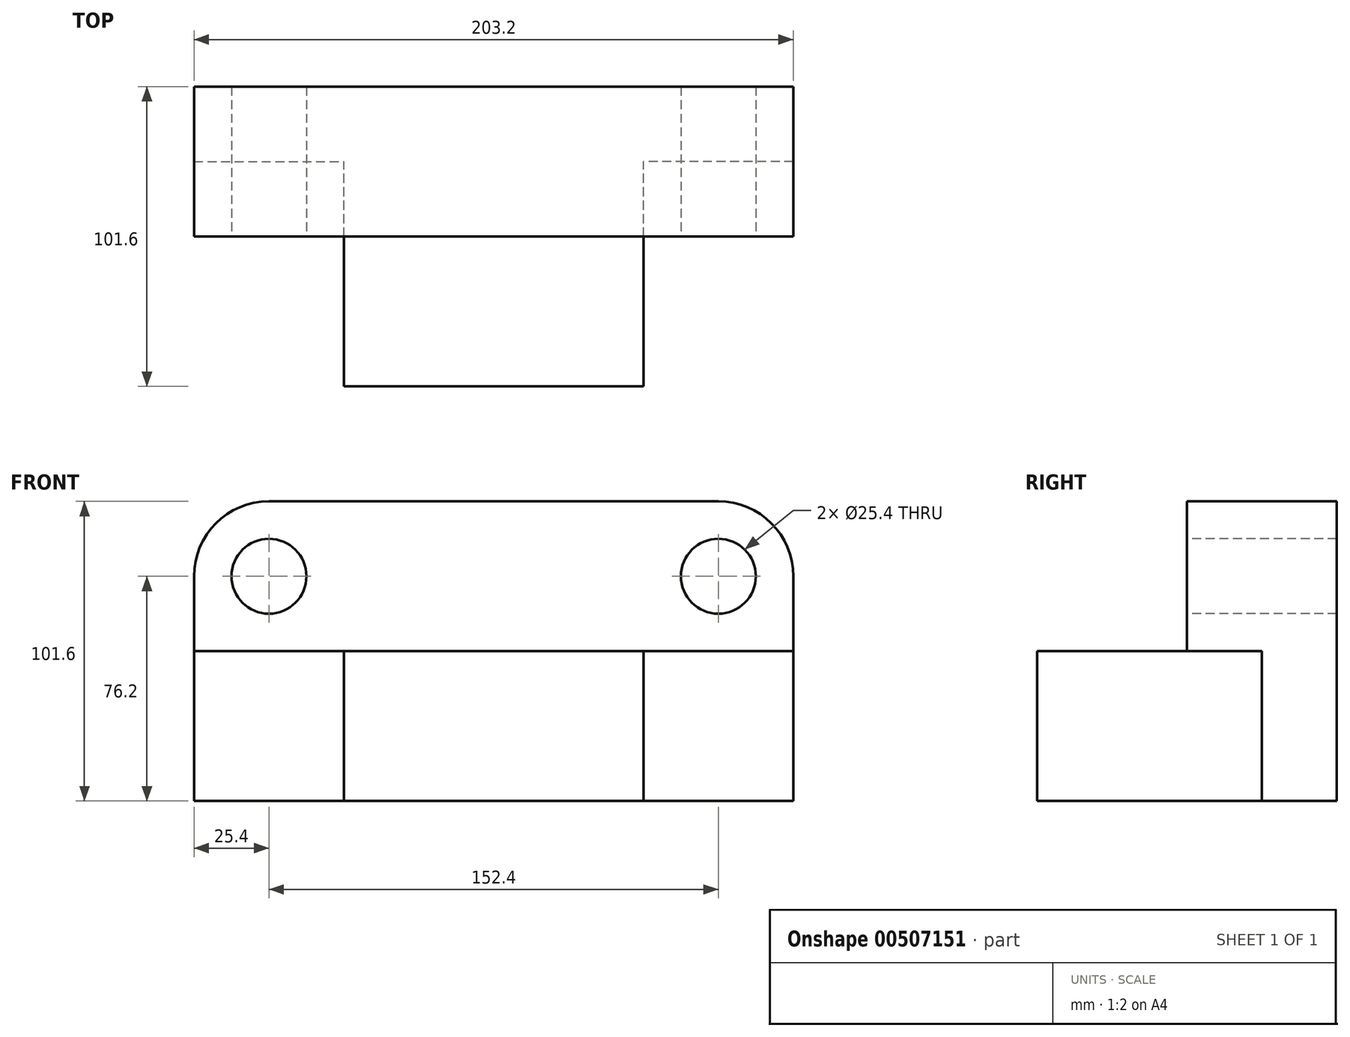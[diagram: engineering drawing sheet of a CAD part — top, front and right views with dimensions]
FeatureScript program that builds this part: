
annotation { "Feature Type Name" : "Feature", "Feature Type Description" : "" }
export const myFeature = defineFeature(function(context is Context, id is Id, definition is map)
    precondition{}
    {
        {
            var Q0;
            Q0=qCreatedBy(makeId("Front.planeOp"),FACE);
            var sketch = newSketch(context, id + "F0", { "sketchPlane" : qUnion([Q0])});
            skLineSegment(sketch, "E0.bottom", {"start": v(0, 0) * mm, "end": v(-101.6, 0) * mm});
            skLineSegment(sketch, "E0.top", {"start": v(0, 50.8) * mm, "end": v(-101.6, 50.8) * mm});
            skLineSegment(sketch, "E0.left", {"start": v(0, 0) * mm, "end": v(0, 50.8) * mm});
            skLineSegment(sketch, "E0.right", {"start": v(-101.6, 0) * mm, "end": v(-101.6, 50.8) * mm});
            skSolve(sketch);
        }
        {
            var Q0;
            Q0=makeQuery(id+"F0.imprint","IMPRINT",FACE,{"disambiguationData":[TD([[makeQuery(id+"F0.imprint","IMPRINT",EDGE,{"derivedFrom":sQuery(id+"F0.wireOp",EDGE,"E0.bottom")}),-1.0]])]});
            extrude(context, id + "F1", {"entities" : qUnion([Q0]), "depth" : 76.2 * mm, "offsetDistance" : 25.4 * mm});
        }
        {
            var Q0;
            Q0=makeQuery(id+"F1.opExtrude","SWEPT_FACE",FACE,{"disambiguationData":[OSD([sQuery(id+"F0.wireOp",EDGE,"E0.left")])]});
            var sketch = newSketch(context, id + "F2", { "sketchPlane" : qUnion([Q0])});
            skLineSegment(sketch, "E1.bottom", {"start": v(0, 0) * mm, "end": v(25.4, 0) * mm});
            skLineSegment(sketch, "E1.top", {"start": v(0, 50.8) * mm, "end": v(25.4, 50.8) * mm});
            skLineSegment(sketch, "E1.left", {"start": v(0, 0) * mm, "end": v(0, 50.8) * mm});
            skLineSegment(sketch, "E1.right", {"start": v(25.4, 0) * mm, "end": v(25.4, 50.8) * mm});
            skSolve(sketch);
        }
        {
            var Q0;
            Q0=makeQuery(id+"F2.imprint","IMPRINT",FACE,{"disambiguationData":[TD([[makeQuery(id+"F2.imprint","IMPRINT",EDGE,{"derivedFrom":sQuery(id+"F2.wireOp",EDGE,"E1.bottom")}),1.0]])]});
            extrude(context, id + "F3", {"entities" : qUnion([Q0]), "operationType" : NewBodyOperationType.ADD, "oppositeDirection" : true, "depth" : 152.4 * mm, "offsetDistance" : 25.4 * mm});
        }
        {
            var Q0;
            Q0=makeQuery(id+"F3.boolean.opBoolean","MERGE",FACE,{"derivedFrom":[makeQuery(id+"F1.opExtrude","SWEPT_FACE",FACE,{"disambiguationData":[OSD([sQuery(id+"F0.wireOp",EDGE,"E0.left")])]}),makeQuery(id+"F3.opExtrude","CAP_FACE",FACE,{"disambiguationData":[OSD([sQuery(id+"F2.wireOp",EDGE,"E1.bottom"),sQuery(id+"F2.wireOp",EDGE,"E1.top"),sQuery(id+"F2.wireOp",EDGE,"E1.left"),sQuery(id+"F2.wireOp",EDGE,"E1.right")])],"isStart":true})]});
            var sketch = newSketch(context, id + "F4", { "sketchPlane" : qUnion([Q0])});
            skLineSegment(sketch, "E2", {"start": v(0, 0) * mm, "end": v(0, 50.8) * mm});
            skLineSegment(sketch, "E3", {"start": v(0, 50.8) * mm, "end": v(25.4, 50.8) * mm});
            skLineSegment(sketch, "E4", {"start": v(25.4, 50.8) * mm, "end": v(25.4, 0) * mm});
            skLineSegment(sketch, "E5", {"start": v(25.4, 0) * mm, "end": v(0, 0) * mm});
            skSolve(sketch);
        }
        {
            var Q0;
            Q0=makeQuery(id+"F4.imprint","IMPRINT",FACE,{"disambiguationData":[TD([[makeQuery(id+"F4.imprint","IMPRINT",EDGE,{"derivedFrom":sQuery(id+"F4.wireOp",EDGE,"E2")}),-1.0]])]});
            extrude(context, id + "F5", {"entities" : qUnion([Q0]), "operationType" : NewBodyOperationType.ADD, "depth" : 50.8 * mm, "offsetDistance" : 25.4 * mm});
        }
        {
            var Q0;
            Q0=makeQuery(id+"F5.boolean.opBoolean","MERGE",FACE,{"derivedFrom":[makeQuery(id+"F3.boolean.opBoolean","MERGE",FACE,{"derivedFrom":[makeQuery(id+"F1.opExtrude","SWEPT_FACE",FACE,{"disambiguationData":[OSD([sQuery(id+"F0.wireOp",EDGE,"E0.top")])]}),makeQuery(id+"F3.opExtrude","SWEPT_FACE",FACE,{"disambiguationData":[OSD([sQuery(id+"F2.wireOp",EDGE,"E1.top")])]})]}),makeQuery(id+"F5.opExtrude","SWEPT_FACE",FACE,{"disambiguationData":[OSD([sQuery(id+"F4.wireOp",EDGE,"E3")])]})]});
            var sketch = newSketch(context, id + "F6", { "sketchPlane" : qUnion([Q0])});
            skLineSegment(sketch, "E6", {"start": v(-152.4, 25.4) * mm, "end": v(50.8, 25.4) * mm});
            skLineSegment(sketch, "E7", {"start": v(50.8, 25.4) * mm, "end": v(50.8, -25.4) * mm});
            skLineSegment(sketch, "E8", {"start": v(50.8, -25.4) * mm, "end": v(-152.4, -25.4) * mm});
            skLineSegment(sketch, "E9", {"start": v(-152.4, -25.4) * mm, "end": v(-152.4, 25.4) * mm});
            skSolve(sketch);
        }
        {
            var Q0;
            {var subQ1=sQuery(id+"F2.wireOp",EDGE,"E1.top");var subQ2=sQuery(id+"F0.wireOp",EDGE,"E0.left");var subQ3=sQuery(id+"F0.wireOp",EDGE,"E0.top");var subQ4=makeQuery(id+"F5.opExtrude","SWEPT_EDGE",EDGE,{"disambiguationData":[OSD([subQ3,subQ2,subQ1,sQuery(id+"F4.wireOp",EDGE,"E2"),sQuery(id+"F4.wireOp",EDGE,"E3")])]});Q0=makeQuery(id+"F6.imprint","IMPRINT",FACE,{"disambiguationData":[TD([[makeQuery(id+"F6.imprint","IMPRINT",EDGE,{"derivedFrom":subQ4}),1.0]])]});}
            var Q1;
            {var subQ3=sQuery(id+"F0.wireOp",EDGE,"E0.top");var subQ6=makeQuery(id+"F3.opExtrude","SWEPT_EDGE",EDGE,{"disambiguationData":[OSD([subQ3,sQuery(id+"F0.wireOp",EDGE,"E0.left"),sQuery(id+"F2.wireOp",EDGE,"E1.top"),sQuery(id+"F2.wireOp",EDGE,"E1.left")])]});Q1=makeQuery(id+"F6.imprint","IMPRINT",FACE,{"disambiguationData":[TD([[makeQuery(id+"F6.imprint","IMPRINT",EDGE,{"derivedFrom":subQ6}),-1.0]])]});}
            var Q2;
            {var subQ10=sQuery(id+"F6.wireOp",EDGE,"E6");Q2=makeQuery(id+"F6.imprint","IMPRINT",FACE,{"disambiguationData":[TD([[makeQuery(id+"F6.imprint","IMPRINT",EDGE,{"derivedFrom":subQ10}),-1.0]])]});}
            extrude(context, id + "F7", {"entities" : qUnion([Q0, Q1, Q2]), "operationType" : NewBodyOperationType.ADD, "depth" : 50.8 * mm, "offsetDistance" : 25.4 * mm});
        }
        {
            var Q0;
            Q0=makeQuery(id+"F7.opExtrude","CAP_EDGE",EDGE,{"disambiguationData":[OSD([sQuery(id+"F6.wireOp",EDGE,"E7")])],"isStart":false});
            var Q1;
            Q1=makeQuery(id+"F7.opExtrude","CAP_EDGE",EDGE,{"disambiguationData":[OSD([sQuery(id+"F6.wireOp",EDGE,"E9")])],"isStart":false});
            fillet(context, id + "F8", {"entities" : qUnion([Q0, Q1]), "radius" : 25.4 * mm, "tangentPropagation" : true, "allowEdgeOverflow" : false});
        }
        {
            var Q0;
            Q0=makeQuery(id+"F7.opExtrude","SWEPT_FACE",FACE,{"disambiguationData":[OSD([sQuery(id+"F6.wireOp",EDGE,"E8")])]});
            var sketch = newSketch(context, id + "F9", { "sketchPlane" : qUnion([Q0])});
            skCircle(sketch, "E10", {"center": v(-127, 76.2) * mm, "radius": 12.7 * mm});
            skCircle(sketch, "E11", {"center": v(25.4, 76.2) * mm, "radius": 12.7 * mm});
            skSolve(sketch);
        }
        {
            var Q0;
            Q0=makeQuery(id+"F9.imprint","IMPRINT",FACE,{"disambiguationData":[TD([[makeQuery(id+"F9.imprint","IMPRINT",EDGE,{"derivedFrom":sQuery(id+"F9.wireOp",EDGE,"E10")}),1.0]])]});
            extrude(context, id + "F10", {"entities" : qUnion([Q0]), "operationType" : NewBodyOperationType.REMOVE, "oppositeDirection" : true, "depth" : 50.8 * mm, "offsetDistance" : 25.4 * mm});
        }
        {
            var Q0;
            Q0=makeQuery(id+"F7.opExtrude","SWEPT_FACE",FACE,{"disambiguationData":[OSD([sQuery(id+"F6.wireOp",EDGE,"E8")])]});
            var sketch = newSketch(context, id + "F11", { "sketchPlane" : qUnion([Q0])});
            skCircle(sketch, "E12", {"center": v(25.4, 76.2) * mm, "radius": 12.7 * mm});
            skSolve(sketch);
        }
        {
            var Q0;
            Q0=makeQuery(id+"F11.imprint","IMPRINT",FACE,{"disambiguationData":[TD([[makeQuery(id+"F11.imprint","IMPRINT",EDGE,{"derivedFrom":sQuery(id+"F11.wireOp",EDGE,"E12")}),1.0]])]});
            extrude(context, id + "F12", {"entities" : qUnion([Q0]), "operationType" : NewBodyOperationType.REMOVE, "oppositeDirection" : true, "depth" : 50.8 * mm, "offsetDistance" : 25.4 * mm});
        }
    });
